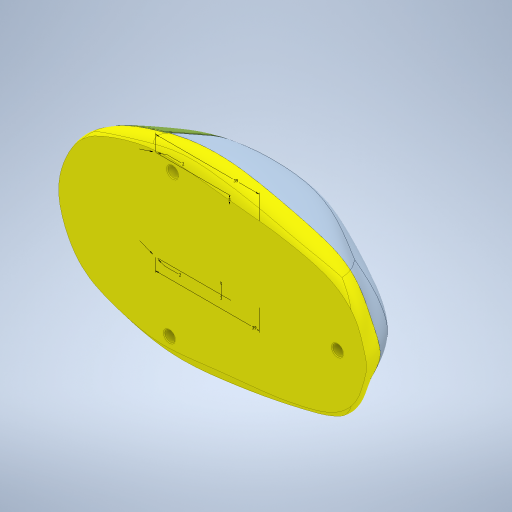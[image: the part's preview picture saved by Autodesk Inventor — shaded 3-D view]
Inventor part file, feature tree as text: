
AUTODESK INVENTOR PART (.ipt)
format: ipt  version: 2023 (Build 270158000, 158)  size: 3,661,312 bytes
history: native  units: mm
features: sketch x15, extrude x8, plane x7, other x5, split x2, thicken_offset x2, sweep x1, fillet x1, hole x1, projected_geometry x1
ambient origin geometry x8: Origin, YZ Plane, XZ Plane, XY Plane, X Axis, Y Axis, Z Axis, Center Point
bodies: Solid1 (feature_tree), Solid3 (feature_tree), Solid6 (feature_tree), Solid2 (feature_tree), Solid4 (feature_tree), Solid5 (feature_tree)
feature tree (43):
  plane  "Work Plane1"
  plane  "Work Plane2"
  split  "Split1"
  split  "Split2"
  sweep  "Sweep1"
  extrude  "Extrusion1"  TaperAngle=0.0deg  [1 undecoded]
  extrude  "Extrusion2"  Depth=1.0mm
  extrude  "Extrusion3"  Depth=20.0mm
  thicken_offset  "Thicken1"
  thicken_offset  "Thicken2"
  extrude  "Extrusion4"  Depth=20.0mm
  fillet  "Fillet1"  Radius=3.0mm
  hole  "Hole1"  [1 undecoded]
  plane  "Work Plane3"
  extrude  "Extrusion5"  Depth=1.3mm TaperAngle=0.0deg
  extrude  "Extrusion6"  Depth=1.0mm
  sketch  "Sketch9"  dims[d21=15.0mm d22=0.5mm]
  extrude  "Extrusion7"  Depth=0.5mm
  other  "Snap Fit1"
  plane  "Work Plane4"
  plane  "Work Plane5"
  other  "Lip1"
  other  "Lip2"
  plane  "Work Plane6"
  sketch  "Sketch12"  dims[d27=1.0mm]
  other  "Boss1"
  other  "Boss2"
  extrude  "Extrusion9"  Depth=1.0mm
  plane  "Work Plane7"
  sketch  "Sketch15"  dims[d29=30.0mm d30=48.0mm d31=27.0mm d32=8.0mm d33=-4.363323mm d34=4.0mm d35=4.0mm d36=4.0mm d37=9.0mm d38=9.0mm d39=2.0mm d40=10.0mm d41=4.0mm d42=2.0mm d43=90.0deg d44=15.0mm d45=20.594885mm d46=0.0mm d47=2.5mm d48=2.5mm d49=10.0mm d50=0.0mm d51=1.5mm d52=1.5mm d53=1.5mm d54=0.0mm d55=20.0mm d56=7.0mm d57=1.3mm d58=4.0mm d59=1.5mm d60=0.0mm d61=7.0mm d62=10.0mm d63=1.35mm d64=1.2mm d65=0.7mm d66=0.7mm d67=3.0mm d68=3.0mm d69=0.5mm d70=0.5mm d71=12.217305mm d72=3.490659mm d73=35.0mm d74=-4.0mm d75=1.0mm d76=0.65mm d77=0.0mm d78=0.0mm d79=0.0mm d80=0.0mm d81=1.0mm d82=0.65mm d83=0.0mm d84=0.0mm d85=0.0mm d86=0.0mm d87=8.0mm d88=45.0mm d89=27.0mm d90=54.0mm d91=62.0mm d92=0.3mm d93=0.0mm d94=4.0mm d95=1.3mm d96=0.5mm d97=3.0mm d98=1.25mm d99=2.2mm d100=0.0mm d101=0.0mm d102=0.0mm d103=0.0mm d104=90.0deg d105=20.0mm d107=2.0mm d108=2.0mm d109=10.0mm d110=0.0mm d111=1.745329mm d112=0.436332mm d113=0.0mm d114=0.0mm d115=0.0mm d116=360.0deg d117=0.5mm d118=0.0mm d119=3.0mm d120=1.0mm d121=10.0mm d122=0.174533mm d123=0.174533mm d124=20.0mm d126=2.0mm d127=2.0mm d128=10.0mm d129=0.0mm d130=1.745329mm d131=0.436332mm d132=0.0mm d133=0.0mm d134=0.0mm d135=360.0deg d144=0.8mm d145=1.0mm d146=1.0mm d147=6.0mm d148=0.0mm d149=0.0mm d150=-12.0mm d151=2.0mm d152=2.0mm d153=3.0mm d154=39.0mm d155=3.0mm d156=39.0mm d142=0.5mm d143=0.872665mm d157=0.5mm d158=0.872665mm d159=0.5mm d160=0.872665mm]
  sketch  "3D Sketch1"
  sketch  "Sketch1"  dims[d0=14.0mm d1=-14.0mm d2=14.0mm]
  sketch  "Sketch2"  dims[d3=1.3mm d4=0.0mm d5=0.0mm]
  sketch  "Sketch3"  dims[d6=1.0mm d7=1.0mm]
  sketch  "Sketch4"  dims[d8=2.3mm d9=20.0mm]
  sketch  "Sketch5"  dims[d10=25.0mm d11=0.0mm d12=20.0mm d13=3.0mm]
  sketch  "Sketch6"  dims[d14=3.0mm d15=5.0mm]
  sketch  "Sketch7"  dims[d16=6.0mm d17=1.3mm d18=0.0mm]
  sketch  "Sketch8"  dims[d19=30.0mm d20=1.0mm]
  projected_geometry  "Projected Loop1"
  sketch  "Sketch10"  dims[d23=0.0mm d24=0.0mm d25=1.0mm]
  sketch  "Sketch11"  dims[d26=1.0mm]
  sketch  "Sketch14"  dims[d28=1.0mm]
note: 2 required parameter values undecoded (feature->parameter linkage not recoverable at this tier; creation-order binding heuristic only, values carry confidence <= 0.55)
